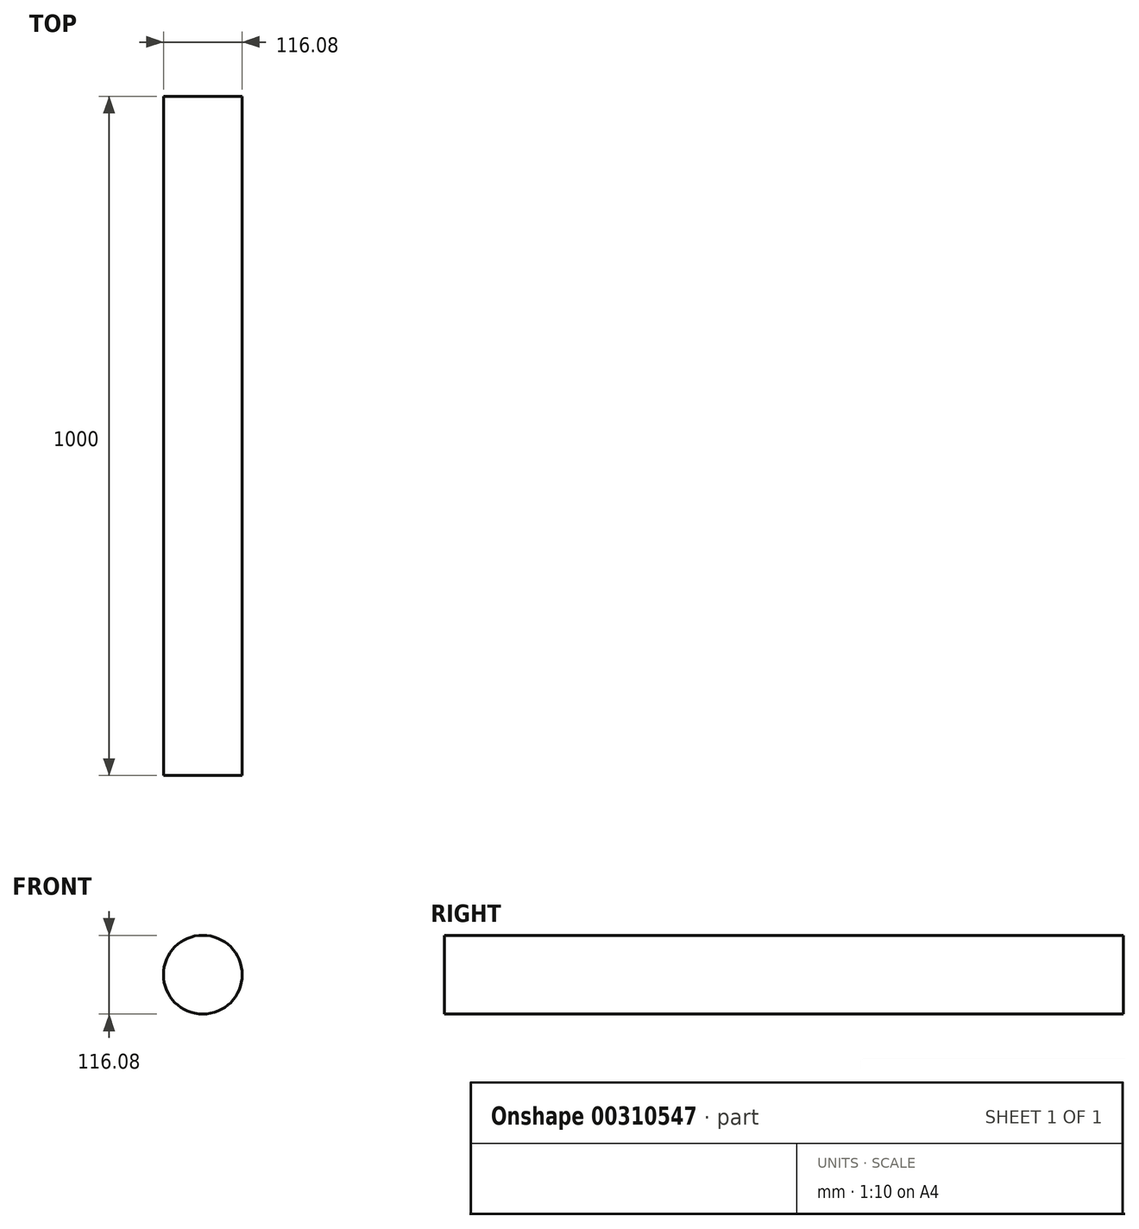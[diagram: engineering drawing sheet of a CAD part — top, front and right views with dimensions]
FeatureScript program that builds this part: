
annotation { "Feature Type Name" : "Feature", "Feature Type Description" : "" }
export const myFeature = defineFeature(function(context is Context, id is Id, definition is map)
    precondition{}
    {
        {
            var Q0;
            Q0=qCreatedBy(makeId("Front.planeOp"),FACE);
            var sketch = newSketch(context, id + "F0", { "sketchPlane" : qUnion([Q0])});
            skCircle(sketch, "E0", {"center": v(0, 0) * mm, "radius": 58.04 * mm});
            skSolve(sketch);
        }
        {
            var Q0;
            Q0=makeQuery(id+"F0.imprint","IMPRINT",FACE,{"disambiguationData":[TD([[makeQuery(id+"F0.imprint","IMPRINT",EDGE,{"derivedFrom":sQuery(id+"F0.wireOp",EDGE,"E0")}),1.0]])]});
            extrude(context, id + "F1", {"entities" : qUnion([Q0]), "depth" : 1000 * mm});
        }
    });
